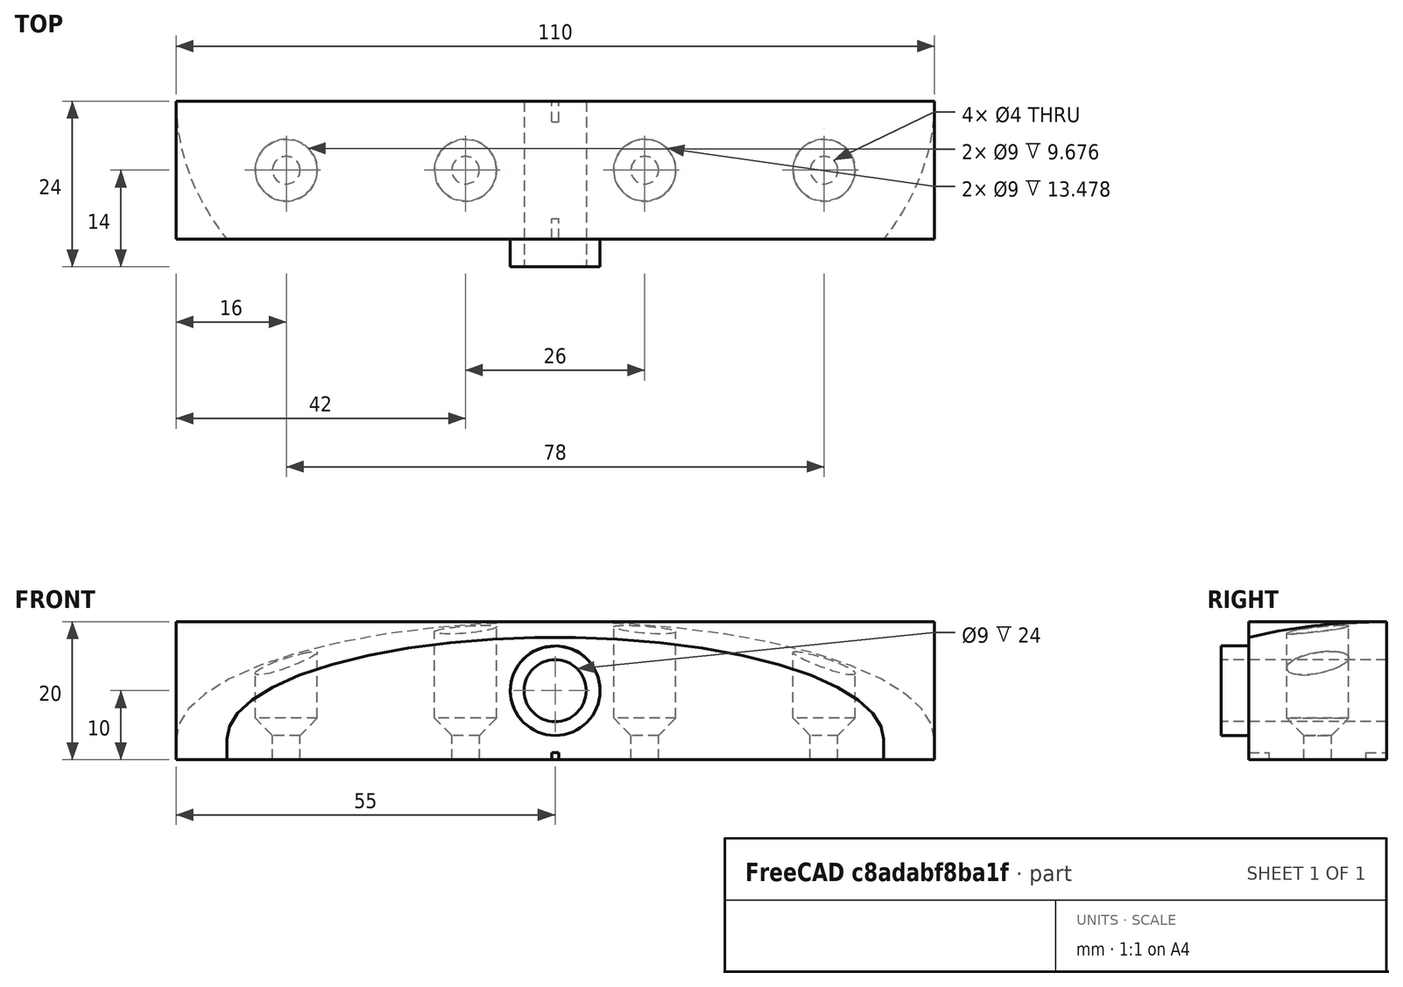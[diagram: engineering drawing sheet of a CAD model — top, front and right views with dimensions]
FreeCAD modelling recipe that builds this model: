
FCSTD DOCUMENT  (FreeCAD 0.18R4 (GitTag))
Label: External Support
License: All rights reserved
LicenseURL: http://en.wikipedia.org/wiki/All_rights_reserved
objects: Part::MultiFuse×5, Part::Cylinder×4, Part::Box×3, Part::Cut×3, Part::Feature×2, Part::Extrusion×2, Part::Ellipsoid×1, Part::FeaturePython×1, Part::Chamfer×1
note: 22 computed .brp shape members not serialized (recipe doc carries the construction recipe); baked Part::Feature solids carry a one-line shape summary decoded from their .brp

FEATURE [Part::Box] Box001  label="Boundinbox"
  AttacherType = Attacher::AttachEngine3D
  Height = 20
  Length = 110
  Placement = pos=(-55,-10,0) rot=(0,0,1;0rad)
  Width = 20
FEATURE [Part::Ellipsoid] Ellipsoid
  Angle1 = 0
  Angle2 = 30
  Angle3 = 180
  AttacherType = Attacher::AttachEngine3D
  Placement = pos=(0,10,3) rot=(1,0,0;1.5708rad)
  Radius1 = 40
  Radius2 = 55
  Radius3 = 17
FEATURE [Part::Box] Box002  label="Signal1"
  AttacherType = Attacher::AttachEngine3D
  Height = 1
  Length = 1
  Placement = pos=(-0.5,-10,0) rot=(0,0,1;0rad)
  Width = 3
FEATURE [Part::Cylinder] Cylinder  label="Hole"
  Angle = 360
  AttacherType = Attacher::AttachEngine3D
  Height = 24
  Placement = pos=(0,10,10) rot=(1,0,0;1.5708rad)
  Radius = 4.5
FEATURE [Part::Box] Box003  label="Signal2"
  AttacherType = Attacher::AttachEngine3D
  Height = 1
  Length = 1
  Placement = pos=(-0.5,7,0) rot=(0,0,1;0rad)
  Width = 3
FEATURE [Part::Cylinder] Cylinder001  label="Cylinder"
  Angle = 360
  AttacherType = Attacher::AttachEngine3D
  Height = 24
  Placement = pos=(0,10,10) rot=(1,0,0;1.5708rad)
  Radius = 6.5
FEATURE [Part::MultiFuse] Fusion001
  Refine = true
  Shapes = -> [Cylinder001,Ellipsoid]
FEATURE [Part::Cut] Cut001  label="Ellipsoid001"
  Base = -> Fusion001
  Refine = true
  Tool = -> Cylinder
FEATURE [Part::Cylinder] Cylinder002  label="Cylinder003"
  Angle = 360
  AttacherType = Attacher::AttachEngine3D
  Height = 25
  Radius = 2
FEATURE [Part::Cylinder] Cylinder003  label="Cylinder002"
  Angle = 360
  AttacherType = Attacher::AttachEngine3D
  Height = 20
  Placement = pos=(0,0,6) rot=(0,0,1;0rad)
  Radius = 4.5
FEATURE [Part::MultiFuse] Fusion003  label="screw hole 1"
  Refine = true
  Shapes = -> [Cylinder003,Cylinder002]
FEATURE [Part::FeaturePython] Array  # Draft array (typed FeaturePython)
  Angle = 360
  ArrayType = 0
  Axis = (0,0,1)
  Base = -> Fusion003
  Center = (0,0,0)
  Fuse = false
  IntervalAxis = (0,0,0)
  IntervalX = (26,0,0)
  IntervalY = (0,0,0)
  IntervalZ = (0,0,0)
  NumberPolar = 1
  NumberX = 4
  NumberY = 1
  NumberZ = 1
  Placement = pos=(-39,0,0) rot=(0,0,1;0rad)
FEATURE [Part::Feature] Face
  Placement = pos=(0,10,3) rot=(1,0,0;1.5708rad)
  shape: bbox 55 x 20 x 2e-07 mm, 1 faces, 0 solids (baked)
FEATURE [Part::Feature] Face001
  Placement = pos=(0,10,3) rot=(1,0,0;1.5708rad)
  shape: bbox 55 x 20 x 2e-07 mm, 1 faces, 0 solids (baked)
FEATURE [Part::Extrusion] Extrusion001
  Base = -> Face001
  Dir = (0,0,-3)
  DirMode = 0
  FaceMakerClass = Part::FaceMakerBullseye
  LengthFwd = 0
  LengthRev = 0
  Solid = true
  Symmetric = false
FEATURE [Part::Extrusion] Extrusion
  Base = -> Face
  Dir = (0,0,-3)
  DirMode = 0
  FaceMakerClass = Part::FaceMakerBullseye
  LengthFwd = 0
  LengthRev = 0
  Solid = true
  Symmetric = false
FEATURE [Part::MultiFuse] Fusion004  label="Solid"
  Refine = true
  Shapes = -> [Extrusion001,Extrusion]
FEATURE [Part::MultiFuse] Fusion005  label="References"
  Refine = true
  Shapes = -> [Box002,Box003]
FEATURE [Part::Cut] Cut  label="Base"
  Base = -> Fusion004
  Refine = true
  Tool = -> Fusion005
FEATURE [Part::MultiFuse] Fusion002  label="Support"
  Refine = true
  Shapes = -> [Cut001,Cut]
FEATURE [Part::Cut] Cut002  label="External Support"
  Base = -> Fusion002
  Refine = true
  Tool = -> Array
FEATURE [Part::Chamfer] Chamfer
  Base = -> Cut002
  Edges = 4 edges r=2.49: [Edge71,Edge72,Edge73,Edge74]
